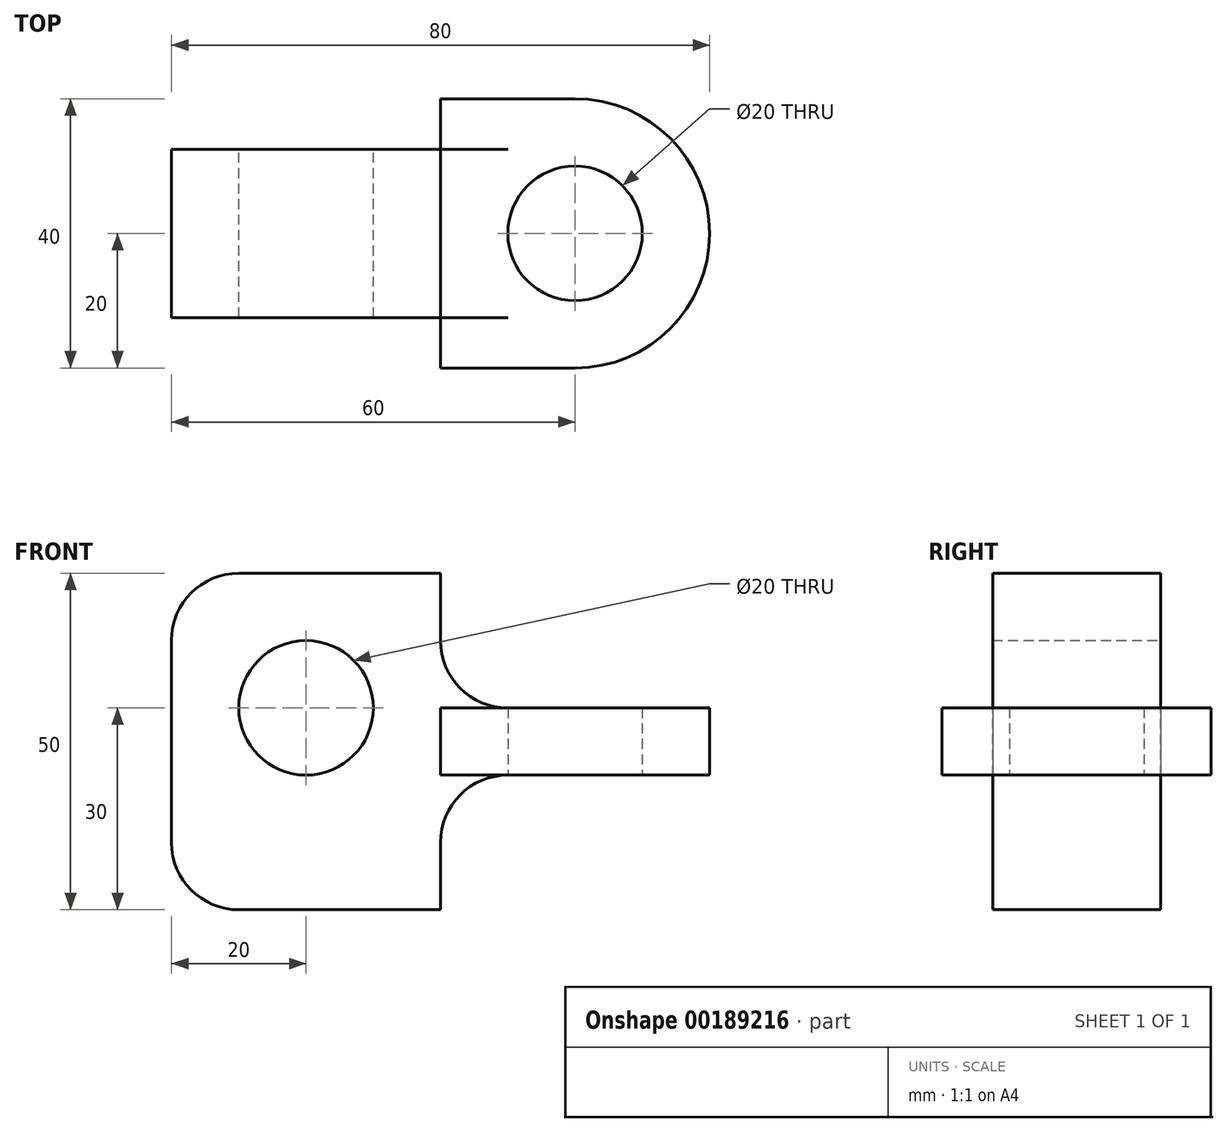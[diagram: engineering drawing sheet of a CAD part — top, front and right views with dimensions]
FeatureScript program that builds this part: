
annotation { "Feature Type Name" : "Feature", "Feature Type Description" : "" }
export const myFeature = defineFeature(function(context is Context, id is Id, definition is map)
    precondition{}
    {
        {
            var Q0;
            Q0=qCreatedBy(makeId("Top.planeOp"),FACE);
            var sketch = newSketch(context, id + "F0", { "sketchPlane" : qUnion([Q0])});
            skCircle(sketch, "E0", {"center": v(0, 0) * mm, "radius": 10 * mm});
            skArc(sketch, "E1", {"start": v(0, -20) * mm, "mid": v(20, 0) * mm, "end": v(0, 20) * mm});
            skLineSegment(sketch, "E2", {"start": v(0, 20) * mm, "end": v(-20, 20) * mm});
            skLineSegment(sketch, "E3", {"start": v(-20, 20) * mm, "end": v(-20, -20) * mm});
            skLineSegment(sketch, "E4", {"start": v(-20, -20) * mm, "end": v(0, -20) * mm});
            skPoint(sketch, "E5.orphan", {"position": v(0, -20) * mm});
            skSolve(sketch);
        }
        {
            var Q0;
            Q0=makeQuery(id+"F0.imprint","IMPRINT",FACE,{"disambiguationData":[TD([[makeQuery(id+"F0.imprint","IMPRINT",EDGE,{"derivedFrom":sQuery(id+"F0.wireOp",EDGE,"E0")}),-1.0]])]});
            extrude(context, id + "F1", {"entities" : qUnion([Q0]), "endBound" : BoundingType.SYMMETRIC, "depth" : 10 * mm});
        }
        {
            var Q0;
            Q0=qCreatedBy(makeId("Front.planeOp"),FACE);
            var sketch = newSketch(context, id + "F2", { "sketchPlane" : qUnion([Q0])});
            skLineSegment(sketch, "E6", {"start": v(-20, 15) * mm, "end": v(-20, 25) * mm});
            skLineSegment(sketch, "E7", {"start": v(-20, 25) * mm, "end": v(-50, 25) * mm});
            skLineSegment(sketch, "E8", {"start": v(-60, 15) * mm, "end": v(-60, -15) * mm});
            skLineSegment(sketch, "E9", {"start": v(-50, -25) * mm, "end": v(-20, -25) * mm});
            skLineSegment(sketch, "E10", {"start": v(-20, -25) * mm, "end": v(-20, -15) * mm});
            skLineSegment(sketch, "E11.0", {"start": v(-20, 5) * mm, "end": v(-20, -5) * mm});
            skArc(sketch, "E12.filletArc", {"start": v(-20, 15) * mm, "mid": v(-17.07, 7.93) * mm, "end": v(-10, 5) * mm});
            skArc(sketch, "E13.filletArc", {"start": v(-10, -5) * mm, "mid": v(-17.07, -7.93) * mm, "end": v(-20, -15) * mm});
            skPoint(sketch, "E14.0.end.orphan", {"position": v(0, 5) * mm});
            skPoint(sketch, "E15.0.end.orphan", {"position": v(0, -5) * mm});
            skPoint(sketch, "E16.visualSharp", {"position": v(-60, 25) * mm});
            skArc(sketch, "E16.filletArc", {"start": v(-50, 25) * mm, "mid": v(-57.07, 22.07) * mm, "end": v(-60, 15) * mm});
            skPoint(sketch, "E17.visualSharp", {"position": v(-60, -25) * mm});
            skArc(sketch, "E17.filletArc", {"start": v(-60, -15) * mm, "mid": v(-57.07, -22.07) * mm, "end": v(-50, -25) * mm});
            skCircle(sketch, "E18", {"center": v(-40, 5) * mm, "radius": 10 * mm});
            skLineSegment(sketch, "E19", {"start": v(-20, 5) * mm, "end": v(-10, 5) * mm});
            skLineSegment(sketch, "E20", {"start": v(-20, -5) * mm, "end": v(-10, -5) * mm});
            skSolve(sketch);
        }
        {
            var Q0;
            Q0=makeQuery(id+"F2.imprint","IMPRINT",FACE,{"disambiguationData":[TD([[makeQuery(id+"F2.imprint","IMPRINT",EDGE,{"derivedFrom":sQuery(id+"F2.wireOp",EDGE,"E6")}),1.0]])]});
            extrude(context, id + "F3", {"entities" : qUnion([Q0]), "operationType" : NewBodyOperationType.ADD, "endBound" : BoundingType.SYMMETRIC, "depth" : 25 * mm});
        }
    });
